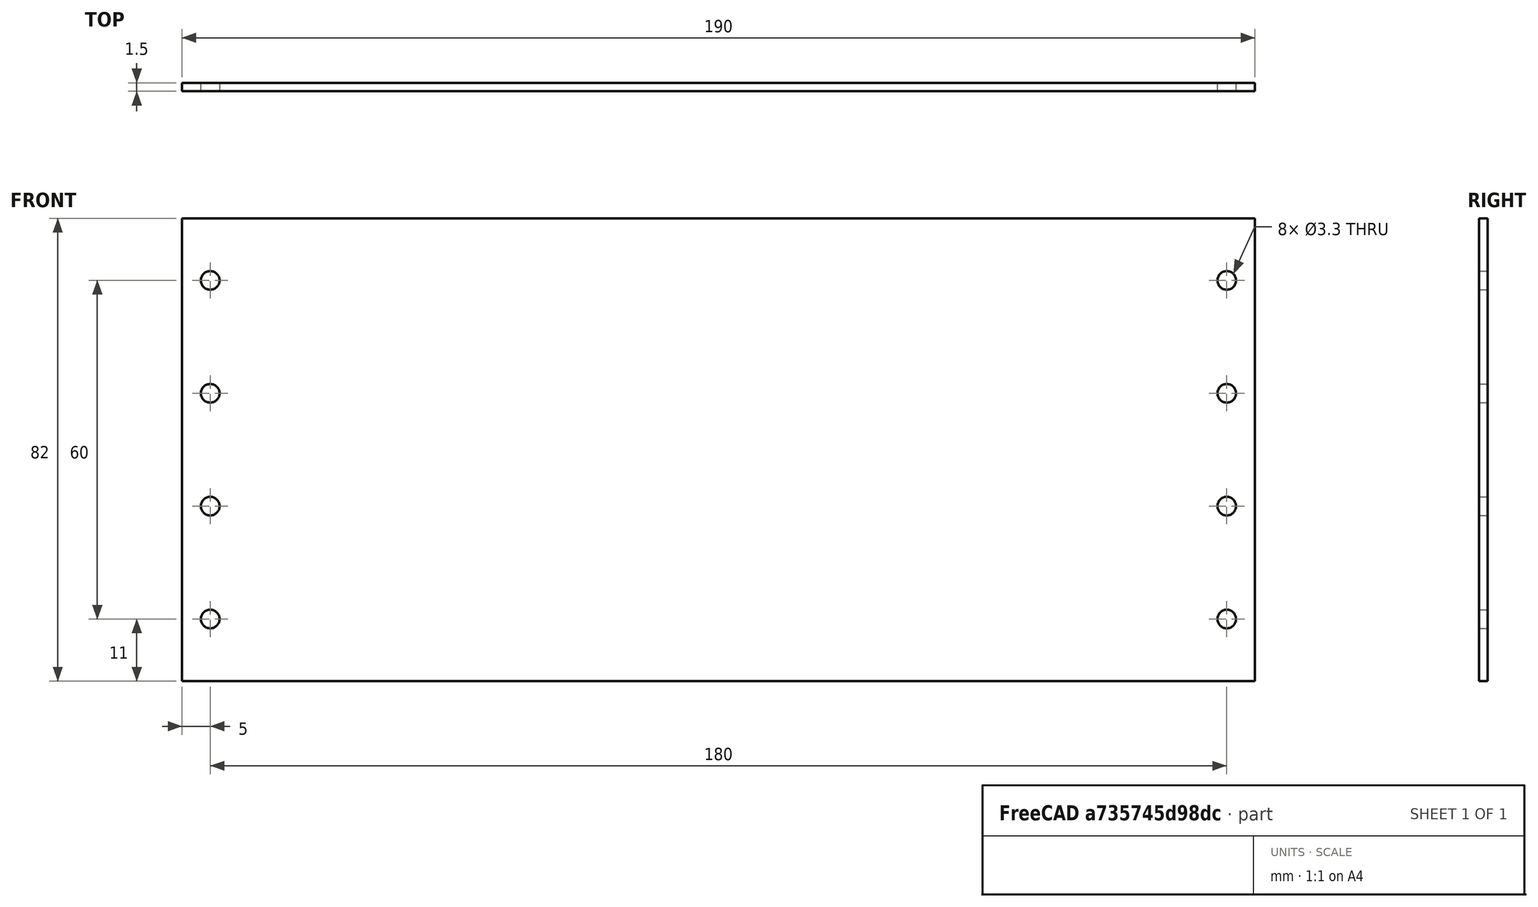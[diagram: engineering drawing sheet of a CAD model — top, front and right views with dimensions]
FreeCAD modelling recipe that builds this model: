
FCSTD DOCUMENT  (FreeCAD 1.0R39109 (Git))
Label: wall_frontal_template
License: All rights reserved
LicenseURL: https://en.wikipedia.org/wiki/All_rights_reserved
objects: PartDesign::Body×2, Sketcher::SketchObject×1, PartDesign::Pad×1
note: 7 computed .brp shape members not serialized (recipe doc carries the construction recipe); baked Part::Feature solids carry a one-line shape summary decoded from their .brp

FEATURE [Sketcher::SketchObject] Sketch
  ArcFitTolerance = 1e-06
  AttachmentSupport = -> [XZ_Plane]
  FullyConstrained = true
  MakeInternals = false
  MapMode = 5
  Placement = pos=(0,0,0) rot=(1,0,0;1.5708rad)
  sketch-geometry (18):
    g0: LineSegment StartX=-95 StartY=41 StartZ=0 EndX=-95 EndY=-41 EndZ=0
    g1: LineSegment StartX=-95 StartY=-41 StartZ=0 EndX=95 EndY=-41 EndZ=0
    g2: LineSegment StartX=95 StartY=-41 StartZ=0 EndX=95 EndY=41 EndZ=0
    g3: LineSegment StartX=95 StartY=41 StartZ=0 EndX=-95 EndY=41 EndZ=0
    g4: GeomPoint [constr] X=0 Y=0 Z=0
    g5: LineSegment [constr] StartX=-95 StartY=40 StartZ=0 EndX=-95 EndY=-40 EndZ=0
    g6: LineSegment [constr] StartX=-95 StartY=-40 StartZ=0 EndX=95 EndY=-40 EndZ=0
    g7: LineSegment [constr] StartX=95 StartY=-40 StartZ=0 EndX=95 EndY=40 EndZ=0
    g8: LineSegment [constr] StartX=95 StartY=40 StartZ=0 EndX=-95 EndY=40 EndZ=0
    g9: GeomPoint [constr] X=0 Y=0 Z=0
    g10: Circle CenterX=90 CenterY=30 CenterZ=0 NormalX=0 NormalY=0 NormalZ=1 AngleXU=0 Radius=1.65
    g11: Circle CenterX=90 CenterY=10 CenterZ=0 NormalX=0 NormalY=0 NormalZ=1 AngleXU=0 Radius=1.65
    g12: Circle CenterX=90 CenterY=-30 CenterZ=0 NormalX=0 NormalY=0 NormalZ=1 AngleXU=0 Radius=1.65
    g13: Circle CenterX=90 CenterY=-10 CenterZ=0 NormalX=0 NormalY=0 NormalZ=1 AngleXU=0 Radius=1.65
    g14: Circle CenterX=-90 CenterY=30 CenterZ=0 NormalX=0 NormalY=0 NormalZ=1 AngleXU=0 Radius=1.65
    g15: Circle CenterX=-90 CenterY=10 CenterZ=0 NormalX=0 NormalY=0 NormalZ=1 AngleXU=0 Radius=1.65
    g16: Circle CenterX=-90 CenterY=-30 CenterZ=0 NormalX=0 NormalY=0 NormalZ=1 AngleXU=0 Radius=1.65
    g17: Circle CenterX=-90 CenterY=-10 CenterZ=0 NormalX=0 NormalY=0 NormalZ=1 AngleXU=0 Radius=1.65
  constraints (42):
    c: Coincident(g0,g1)
    c: Coincident(g1,g2)
    c: Coincident(g2,g3)
    c: Coincident(g3,g0)
    c: Vertical(g0)
    c: Vertical(g2)
    c: Horizontal(g1)
    c: Horizontal(g3)
    c: Symmetric(g2,g0,g4)
    c: Coincident(g4,g-1)
    c: Coincident(g5,g6)
    c: Coincident(g6,g7)
    c: Coincident(g7,g8)
    c: Coincident(g8,g5)
    c: Vertical(g5)
    c: Vertical(g7)
    c: Horizontal(g6)
    c: Horizontal(g8)
    c: Symmetric(g7,g5,g9)
    c: Coincident(g9,g4)
    c: PointOnObject(g6,g2)
    c: DistanceY(g6,g7) = 80
    c: DistanceY(g1,g6) = 1
    c: DistanceX(g1,g1) = 190
    c: Equal(g10,g11)
    c: Radius(g11) = 1.65
    c: DistanceY(g11,g10) = 20
    c: Vertical(g10,g11)
    c: DistanceX(g10,g7) = 5
    c: DistanceY(g10,g7) = 10
    c: Equal(g12,g13)
    c: Radius(g13) = 1.65
    c: Equal(g14,g15)
    c: Radius(g15) = 1.65
    c: Equal(g16,g17)
    c: Radius(g17) = 1.65
    c: Symmetric(g10,g12,g-1)
    c: Symmetric(g13,g11,g-1)
    c: Symmetric(g12,g16,g-2)
    c: Symmetric(g17,g13,g-2)
    c: Symmetric(g11,g15,g-2)
    c: Symmetric(g14,g10,g-2)
FEATURE [PartDesign::Pad] Pad  label="BasePad"
  Direction = (0,-1,2e-16)
  Length = 0.75
  Length2 = 0.75
  Placement = pos=(0,0,0) rot=(1,0,0;1.5708rad)
  Profile = -> Sketch
  ReferenceAxis = -> Sketch [N_Axis]
  Refine = true
  Suppressed = false
  Type = 4
FEATURE [PartDesign::Body] Body  label="wall_fdefault"
  AllowCompound = false
  Group = -> [Sketch,Pad]
  Origin = -> Origin
  Tip = -> Pad
FEATURE [PartDesign::Body] Body001  label="Body"
  AllowCompound = false
  Origin = -> Origin001
